# Revit family: Haworth_Intuity_Parkbench_SeatingTable_AP_PRELIMINARY
name_source: partatom
category: Furniture
revit_build: Autodesk Revit 2018 (Build: 20170223_1515(x64)
units: mm (PartAtom-declared; Revit-internal decimal feet)

## family parameters
Always vertical = Yes
Cut with Voids When Loaded = No
OmniClass Number = 23.40.20.00
OmniClass Title = General Furniture and Specialties
Room Calculation Point = No
Shared = No
Work Plane-Based = No

## types (8) — shared parameters
Actual Height = 730 mm  [stored 2.39501 ft]
Assembly Code = E2020200
Cord Height = 704 mm  [stored 2.30971 ft]
Description = Haworth - Intuity - Parkbench - Seating Table
Glide Finish = Haworth _ Paint _ Allways Black
Manufacturer = Haworth
Max. Depth = 1400 mm  [stored 4.59318 ft]
Max. Width = 2400 mm  [stored 7.87402 ft]
Min. Depth = 1000 mm  [stored 3.28084 ft]
Min. Width = 1600 mm  [stored 5.24934 ft]
Model = WOPBXTXXXX
Size = Verify Final Dim. w/ Haworth
Tray Finish = Haworth _ Paint _ Allways White TROWC
URL = https://www.haworth.com
URL - Product = https://www.haworth.com
Version = 1
Warranty = http://www.haworth.com
With Top = Yes
with Cord = Yes

## per-type parameters (varying)
| type | Actual Depth | Actual Width | Depth | Tray Width | Width | Wood Offset |
| 2400 x 1400 | 1400 mm  [stored 4.59318 ft] | 2400 mm  [stored 7.87402 ft] | 1400 mm  [stored 4.59318 ft] | 1500 mm  [stored 4.92126 ft] | 2400 mm  [stored 7.87402 ft] | 600 mm |
| 2000 x 1400 | 1400 mm  [stored 4.59318 ft] | 2000 mm  [stored 6.56168 ft] | 1400 mm  [stored 4.59318 ft] | 1100 mm | 2000 mm  [stored 6.56168 ft] | 500 mm  [stored 1.64042 ft] |
| 2400 x 1200 | 1200 mm | 2400 mm  [stored 7.87402 ft] | 1200 mm | 1500 mm  [stored 4.92126 ft] | 2400 mm  [stored 7.87402 ft] | 600 mm |
| 2000 x 1200 | 1200 mm | 2000 mm  [stored 6.56168 ft] | 1200 mm | 1100 mm | 2000 mm  [stored 6.56168 ft] | 500 mm  [stored 1.64042 ft] |
| 2400 x 1000 | 1000 mm  [stored 3.28084 ft] | 2400 mm  [stored 7.87402 ft] | 1000 mm  [stored 3.28084 ft] | 1500 mm  [stored 4.92126 ft] | 2400 mm  [stored 7.87402 ft] | 600 mm |
| 2000 x 1000 | 1000 mm  [stored 3.28084 ft] | 2000 mm  [stored 6.56168 ft] | 1000 mm  [stored 3.28084 ft] | 1100 mm | 2000 mm  [stored 6.56168 ft] | 500 mm  [stored 1.64042 ft] |
| 1800 x 1000 | 1000 mm  [stored 3.28084 ft] | 1800 mm  [stored 5.90551 ft] | 1000 mm  [stored 3.28084 ft] | 900 mm  [stored 2.95276 ft] | 1800 mm  [stored 5.90551 ft] | 450 mm  [stored 1.47638 ft] |
| 1600 x 1000 | 1000 mm  [stored 3.28084 ft] | 1600 mm  [stored 5.24934 ft] | 1000 mm  [stored 3.28084 ft] | 700 mm  [stored 2.29659 ft] | 1600 mm  [stored 5.24934 ft] | 400 mm  [stored 1.31234 ft] |

note: [stored X ft] marks values corroborated as IEEE doubles in the binary element streams (Revit-internal decimal feet)

## geometry (parser evidence)
native form markers: Sweep x9
no freeform markers — native parametric forms only
